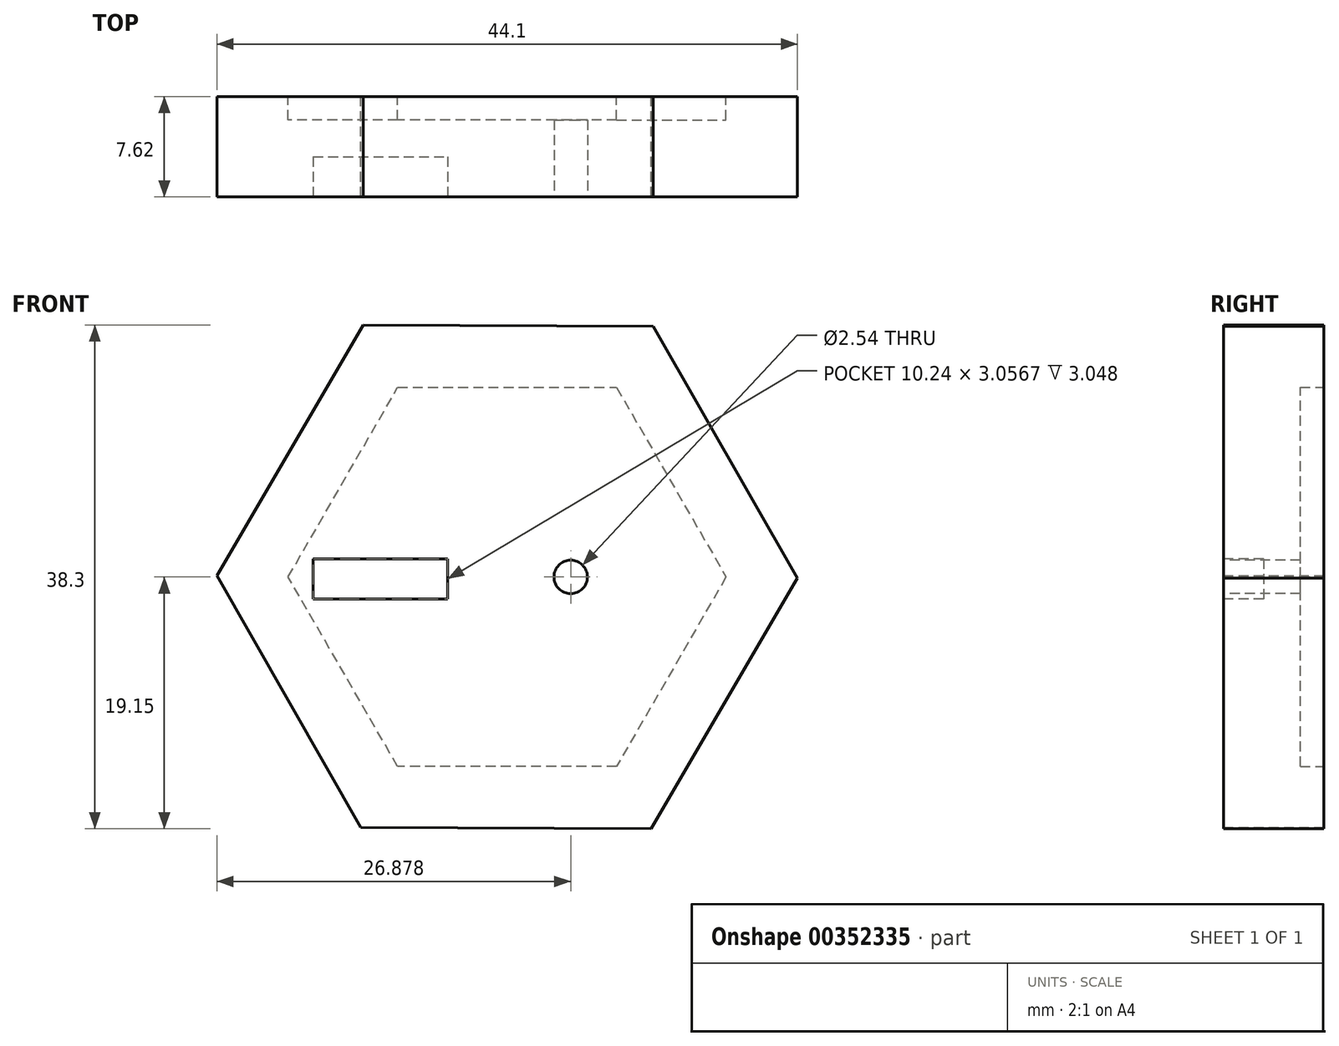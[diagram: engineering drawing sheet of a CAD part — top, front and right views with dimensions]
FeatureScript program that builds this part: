
annotation { "Feature Type Name" : "Feature", "Feature Type Description" : "" }
export const myFeature = defineFeature(function(context is Context, id is Id, definition is map)
    precondition{}
    {
        {
            var Q0;
            Q0=qCreatedBy(makeId("Front.planeOp"),FACE);
            var sketch = newSketch(context, id + "F0", { "sketchPlane" : qUnion([Q0])});
            skCircle(sketch, "E0.cCircle", {"center": v(0, 0) * mm, "radius": 19.1 * mm, "construction": true});
            skLineSegment(sketch, "E0.0", {"start": v(-11.11, -19.05) * mm, "end": v(-22.05, 0.1) * mm});
            skLineSegment(sketch, "E0.1", {"start": v(-22.05, 0.1) * mm, "end": v(-10.94, 19.15) * mm});
            skLineSegment(sketch, "E0.2", {"start": v(-10.94, 19.15) * mm, "end": v(11.11, 19.05) * mm});
            skLineSegment(sketch, "E0.3", {"start": v(11.11, 19.05) * mm, "end": v(22.05, -0.1) * mm});
            skLineSegment(sketch, "E0.4", {"start": v(22.05, -0.1) * mm, "end": v(10.94, -19.15) * mm});
            skLineSegment(sketch, "E0.5", {"start": v(10.94, -19.15) * mm, "end": v(-11.11, -19.05) * mm});
            skPoint(sketch, "E0.0.midPoint", {"position": v(-16.58, -9.48) * mm});
            skSolve(sketch);
        }
        {
            var Q0;
            Q0 = qSketchRegion(id + "F0", true);
            extrude(context, id + "F1", {"entities" : qUnion([Q0]), "depth" : 7.62 * mm});
        }
        {
            var Q0;
            Q0=makeQuery(id+"F1.opExtrude","CAP_FACE",FACE,{"disambiguationData":[OSD([sQuery(id+"F0.wireOp",EDGE,"E0.0"),sQuery(id+"F0.wireOp",EDGE,"E0.1"),sQuery(id+"F0.wireOp",EDGE,"E0.2"),sQuery(id+"F0.wireOp",EDGE,"E0.3"),sQuery(id+"F0.wireOp",EDGE,"E0.4"),sQuery(id+"F0.wireOp",EDGE,"E0.5")])],"isStart":false});
            var sketch = newSketch(context, id + "F2", { "sketchPlane" : qUnion([Q0])});
            skCircle(sketch, "E1", {"center": v(4.83, 0) * mm, "radius": 1.27 * mm});
            skSolve(sketch);
        }
        {
            var Q0;
            Q0 = qSketchRegion(id + "F2", true);
            extrude(context, id + "F3", {"entities" : qUnion([Q0]), "operationType" : NewBodyOperationType.REMOVE, "oppositeDirection" : true, "depth" : 25.4 * mm});
        }
        {
            var Q0;
            Q0=makeQuery(id+"F1.opExtrude","CAP_FACE",FACE,{"disambiguationData":[OSD([sQuery(id+"F0.wireOp",EDGE,"E0.0"),sQuery(id+"F0.wireOp",EDGE,"E0.1"),sQuery(id+"F0.wireOp",EDGE,"E0.2"),sQuery(id+"F0.wireOp",EDGE,"E0.3"),sQuery(id+"F0.wireOp",EDGE,"E0.4"),sQuery(id+"F0.wireOp",EDGE,"E0.5")])],"isStart":false});
            var sketch = newSketch(context, id + "F4", { "sketchPlane" : qUnion([Q0])});
            skLineSegment(sketch, "E2.bottom", {"start": v(-14.75, 1.38) * mm, "end": v(-4.5, 1.38) * mm});
            skLineSegment(sketch, "E2.top", {"start": v(-14.75, -1.68) * mm, "end": v(-4.5, -1.68) * mm});
            skLineSegment(sketch, "E2.left", {"start": v(-14.75, 1.38) * mm, "end": v(-14.75, -1.68) * mm});
            skLineSegment(sketch, "E2.right", {"start": v(-4.5, 1.38) * mm, "end": v(-4.5, -1.68) * mm});
            skSolve(sketch);
        }
        {
            var Q0;
            Q0 = qSketchRegion(id + "F4", true);
            extrude(context, id + "F5", {"entities" : qUnion([Q0]), "operationType" : NewBodyOperationType.REMOVE, "oppositeDirection" : true, "depth" : 3.05 * mm});
        }
        {
            var Q0;
            Q0=qCreatedBy(makeId("Front.planeOp"),FACE);
            var sketch = newSketch(context, id + "F6", { "sketchPlane" : qUnion([Q0])});
            skCircle(sketch, "E3.cCircle", {"center": v(0, 0) * mm, "radius": 14.4 * mm, "construction": true});
            skLineSegment(sketch, "E3.0", {"start": v(8.32, -14.4) * mm, "end": v(-8.32, -14.4) * mm});
            skLineSegment(sketch, "E3.1", {"start": v(-8.32, -14.4) * mm, "end": v(-16.64, 0) * mm});
            skLineSegment(sketch, "E3.2", {"start": v(-16.64, 0) * mm, "end": v(-8.32, 14.4) * mm});
            skLineSegment(sketch, "E3.3", {"start": v(-8.32, 14.4) * mm, "end": v(8.32, 14.4) * mm});
            skLineSegment(sketch, "E3.4", {"start": v(8.32, 14.4) * mm, "end": v(16.64, 0) * mm});
            skLineSegment(sketch, "E3.5", {"start": v(16.64, 0) * mm, "end": v(8.32, -14.4) * mm});
            skPoint(sketch, "E3.0.midPoint", {"position": v(0, -14.4) * mm});
            skSolve(sketch);
        }
        {
            var Q0;
            Q0=makeQuery(id+"F6.imprint","IMPRINT",FACE,{"disambiguationData":[TD([[makeQuery(id+"F6.imprint","IMPRINT",EDGE,{"derivedFrom":sQuery(id+"F6.wireOp",EDGE,"E3.0")}),-1.0]])]});
            extrude(context, id + "F7", {"entities" : qUnion([Q0]), "operationType" : NewBodyOperationType.REMOVE, "depth" : 1.78 * mm});
        }
    });
